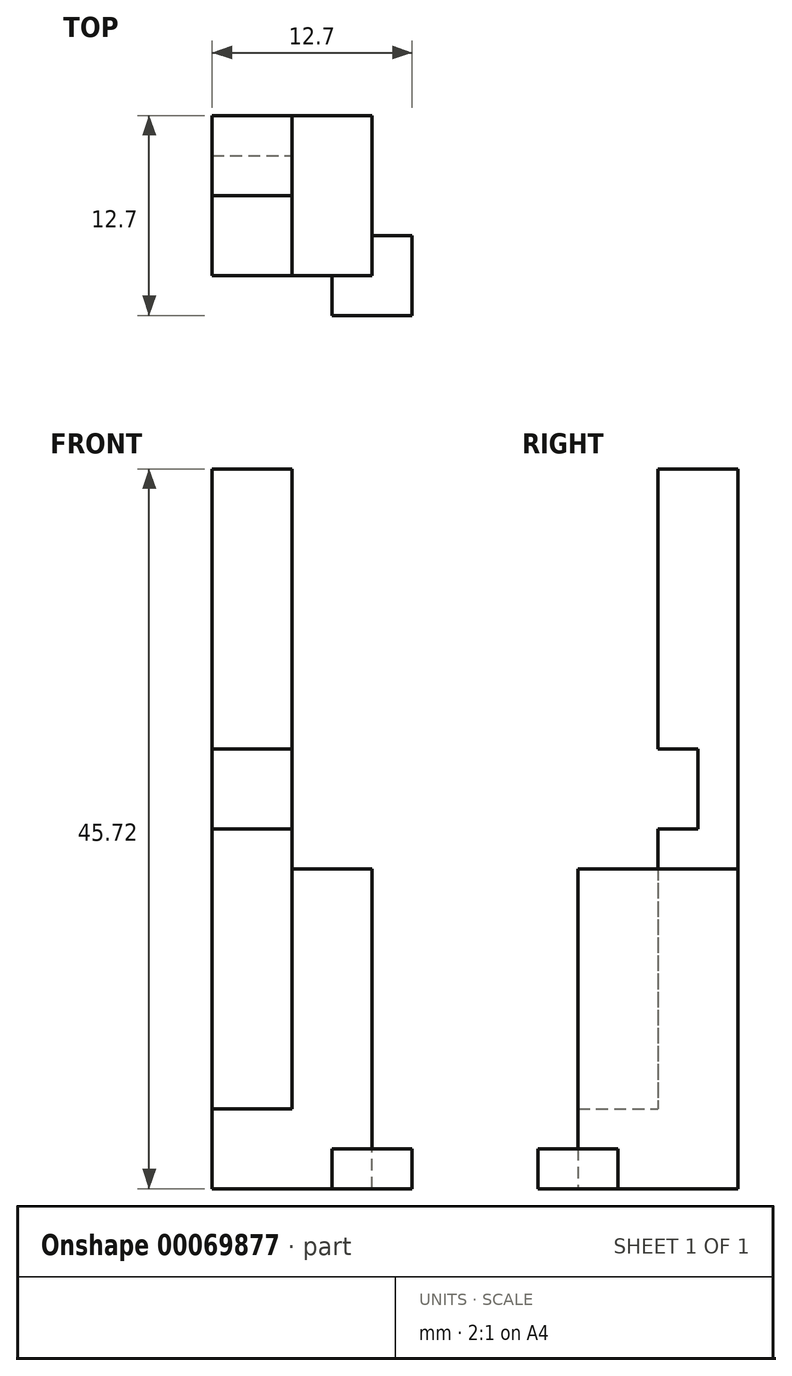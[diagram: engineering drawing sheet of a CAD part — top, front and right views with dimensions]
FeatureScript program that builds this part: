
annotation { "Feature Type Name" : "Feature", "Feature Type Description" : "" }
export const myFeature = defineFeature(function(context is Context, id is Id, definition is map)
    precondition{}
    {
        {
            var Q0;
            Q0=qCreatedBy(makeId("Top.planeOp"),FACE);
            var sketch = newSketch(context, id + "F0", { "sketchPlane" : qUnion([Q0])});
            skLineSegment(sketch, "E0.bottom", {"start": v(0, 0) * mm, "end": v(10.16, 0) * mm});
            skLineSegment(sketch, "E0.top", {"start": v(0, -10.16) * mm, "end": v(10.16, -10.16) * mm});
            skLineSegment(sketch, "E0.left", {"start": v(0, 0) * mm, "end": v(0, -10.16) * mm});
            skLineSegment(sketch, "E0.right", {"start": v(10.16, 0) * mm, "end": v(10.16, -10.16) * mm});
            skSolve(sketch);
        }
        {
            var Q0;
            Q0=qSketchRegion(id+"F0",true);
            extrude(context, id + "F1", {"entities" : qUnion([Q0]), "depth" : 5.08 * mm});
        }
        {
            var Q0;
            Q0=makeQuery(id+"F1.opExtrude","CAP_FACE",FACE,{"disambiguationData":[OSD([sQuery(id+"F0.wireOp",EDGE,"E0.bottom"),sQuery(id+"F0.wireOp",EDGE,"E0.top"),sQuery(id+"F0.wireOp",EDGE,"E0.left"),sQuery(id+"F0.wireOp",EDGE,"E0.right")])],"isStart":true});
            var sketch = newSketch(context, id + "F2", { "sketchPlane" : qUnion([Q0])});
            skLineSegment(sketch, "E1.bottom", {"start": v(7.62, 7.62) * mm, "end": v(12.7, 7.62) * mm});
            skLineSegment(sketch, "E1.top", {"start": v(7.62, 12.7) * mm, "end": v(12.7, 12.7) * mm});
            skLineSegment(sketch, "E1.left", {"start": v(7.62, 7.62) * mm, "end": v(7.62, 12.7) * mm});
            skLineSegment(sketch, "E1.right", {"start": v(12.7, 7.62) * mm, "end": v(12.7, 12.7) * mm});
            skSolve(sketch);
        }
        {
            var Q0;
            Q0=qSketchRegion(id+"F2",true);
            extrude(context, id + "F3", {"entities" : qUnion([Q0]), "operationType" : NewBodyOperationType.ADD, "oppositeDirection" : true, "depth" : 2.54 * mm});
        }
        {
            var Q0;
            Q0=makeQuery(id+"F1.opExtrude","CAP_FACE",FACE,{"disambiguationData":[OSD([sQuery(id+"F0.wireOp",EDGE,"E0.bottom"),sQuery(id+"F0.wireOp",EDGE,"E0.top"),sQuery(id+"F0.wireOp",EDGE,"E0.left"),sQuery(id+"F0.wireOp",EDGE,"E0.right")])],"isStart":false});
            var sketch = newSketch(context, id + "F4", { "sketchPlane" : qUnion([Q0])});
            skLineSegment(sketch, "E2.top", {"start": v(5.08, -5.08) * mm, "end": v(0, -5.08) * mm});
            skLineSegment(sketch, "E2.right", {"start": v(0, 0) * mm, "end": v(0, -5.08) * mm});
            skLineSegment(sketch, "E3", {"start": v(5.08, -5.08) * mm, "end": v(5.08, 0) * mm});
            skLineSegment(sketch, "E4", {"start": v(5.08, 0) * mm, "end": v(0, 0) * mm});
            skSolve(sketch);
        }
        {
            var Q0;
            Q0=qSketchRegion(id+"F4",true);
            extrude(context, id + "F5", {"entities" : qUnion([Q0]), "operationType" : NewBodyOperationType.ADD, "depth" : 40.64 * mm});
        }
        {
            var Q0;
            Q0=makeQuery(id+"F5.opExtrude","SWEPT_FACE",FACE,{"disambiguationData":[OSD([sQuery(id+"F4.wireOp",EDGE,"E3")])]});
            var sketch = newSketch(context, id + "F6", { "sketchPlane" : qUnion([Q0])});
            skLineSegment(sketch, "E5.bottom", {"start": v(-2.54, 22.86) * mm, "end": v(-7.62, 22.86) * mm});
            skLineSegment(sketch, "E5.top", {"start": v(-2.54, 27.94) * mm, "end": v(-7.62, 27.94) * mm});
            skLineSegment(sketch, "E5.left", {"start": v(-2.54, 22.86) * mm, "end": v(-2.54, 27.94) * mm});
            skLineSegment(sketch, "E5.right", {"start": v(-7.62, 22.86) * mm, "end": v(-7.62, 27.94) * mm});
            skSolve(sketch);
        }
        {
            var Q0;
            Q0 = qSketchRegion(id + "F6", true);
            extrude(context, id + "F7", {"entities" : qUnion([Q0]), "operationType" : NewBodyOperationType.REMOVE, "oppositeDirection" : true, "depth" : 25.4 * mm});
        }
        {
            var Q0;
            Q0=makeQuery(id+"F1.opExtrude","CAP_FACE",FACE,{"disambiguationData":[OSD([sQuery(id+"F0.wireOp",EDGE,"E0.bottom"),sQuery(id+"F0.wireOp",EDGE,"E0.top"),sQuery(id+"F0.wireOp",EDGE,"E0.left"),sQuery(id+"F0.wireOp",EDGE,"E0.right")])],"isStart":false});
            var sketch = newSketch(context, id + "F8", { "sketchPlane" : qUnion([Q0])});
            skLineSegment(sketch, "E6.bottom", {"start": v(10.16, 0) * mm, "end": v(5.08, 0) * mm});
            skLineSegment(sketch, "E6.top", {"start": v(10.16, -10.16) * mm, "end": v(5.08, -10.16) * mm});
            skLineSegment(sketch, "E6.left", {"start": v(10.16, 0) * mm, "end": v(10.16, -10.16) * mm});
            skLineSegment(sketch, "E6.right", {"start": v(5.08, 0) * mm, "end": v(5.08, -10.16) * mm});
            skSolve(sketch);
        }
        {
            var Q0;
            Q0 = qSketchRegion(id + "F8", true);
            extrude(context, id + "F9", {"entities" : qUnion([Q0]), "operationType" : NewBodyOperationType.ADD, "depth" : 15.24 * mm});
        }
    });
